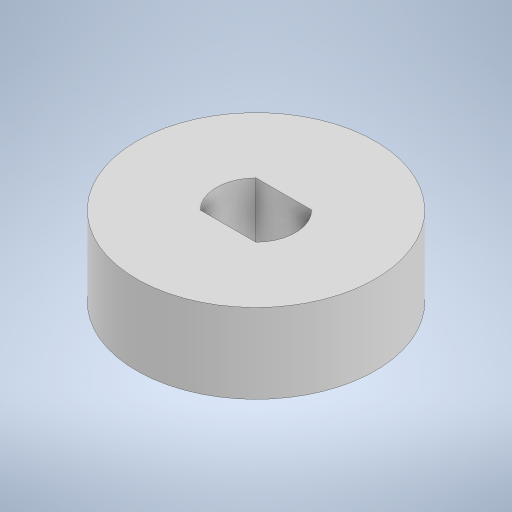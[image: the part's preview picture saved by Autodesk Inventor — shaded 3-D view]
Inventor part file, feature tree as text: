
AUTODESK INVENTOR PART (.ipt)
format: ipt  version: 2023 (Build 270158030, 158C)  size: 215,040 bytes
history: native  units: mm
features: extrude x2, sketch x2
ambient origin geometry x8: Origin, YZ Plane, XZ Plane, XY Plane, X Axis, Y Axis, Z Axis, Center Point
bodies: Solid1 (feature_tree)
feature tree (4):
  extrude  "Extrusion1"  Depth=10.0mm TaperAngle=0.0deg
  extrude  "Extrusion2"  Depth=7.0mm
  sketch  "Sketch1"  dims[d0=30.0mm d1=10.0mm d2=0.0mm]
  sketch  "Sketch2"  dims[d3=7.0mm d4=7.0mm d5=3.5mm d6=3.5mm d7=12.7mm d8=0.0mm]
